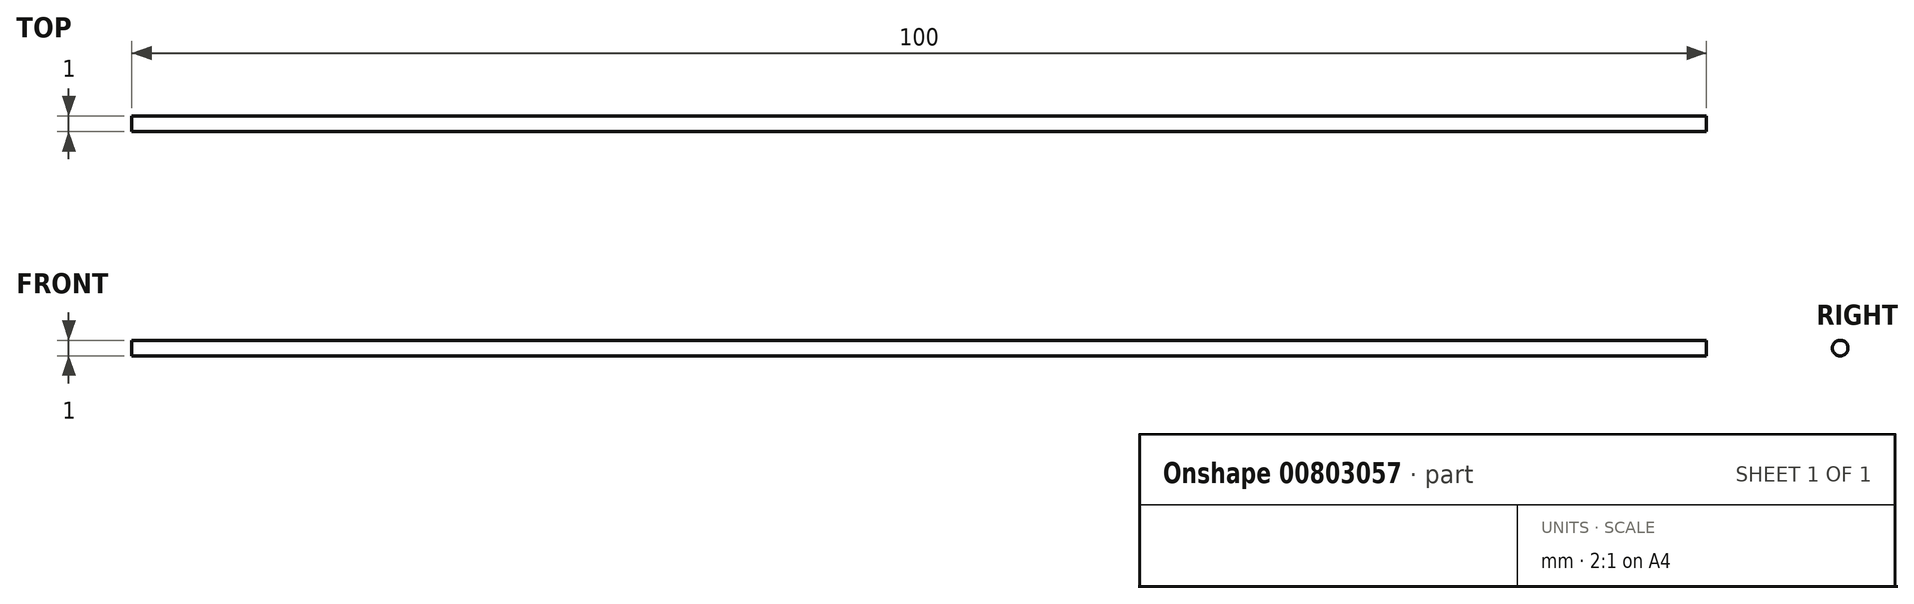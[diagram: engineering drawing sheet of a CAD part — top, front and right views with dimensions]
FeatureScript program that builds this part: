
annotation { "Feature Type Name" : "Feature", "Feature Type Description" : "" }
export const myFeature = defineFeature(function(context is Context, id is Id, definition is map)
    precondition{}
    {
        {
            var Q0;
            Q0=qCreatedBy(makeId("Right.planeOp"),FACE);
            var sketch = newSketch(context, id + "F0", { "sketchPlane" : qUnion([Q0])});
            skCircle(sketch, "E0", {"center": v(0, 0) * mm, "radius": 0.5 * mm});
            skSolve(sketch);
        }
        {
            var Q0;
            Q0 = qSketchRegion(id + "F0", true);
            extrude(context, id + "F1", {"entities" : qUnion([Q0]), "depth" : 100 * mm, "offsetDistance" : 25 * mm, "symmetric" : true});
        }
        {
            var Q0;
            Q0=qCreatedBy(makeId("Top.planeOp"),FACE);
            cPlane(context, id + "F2", {"entities" : qUnion([Q0]), "cplaneType" : CPlaneType.OFFSET, "offset" : 25 * mm, "width" : 150 * mm, "height" : 150 * mm});
        }
        {
            var Q0;
            Q0=qCreatedBy(makeId("Right.planeOp"),FACE);
            cPlane(context, id + "F3", {"entities" : qUnion([Q0]), "cplaneType" : CPlaneType.OFFSET, "offset" : 71.6 * mm, "oppositeDirection" : true, "width" : 150 * mm, "height" : 150 * mm});
        }
    });
